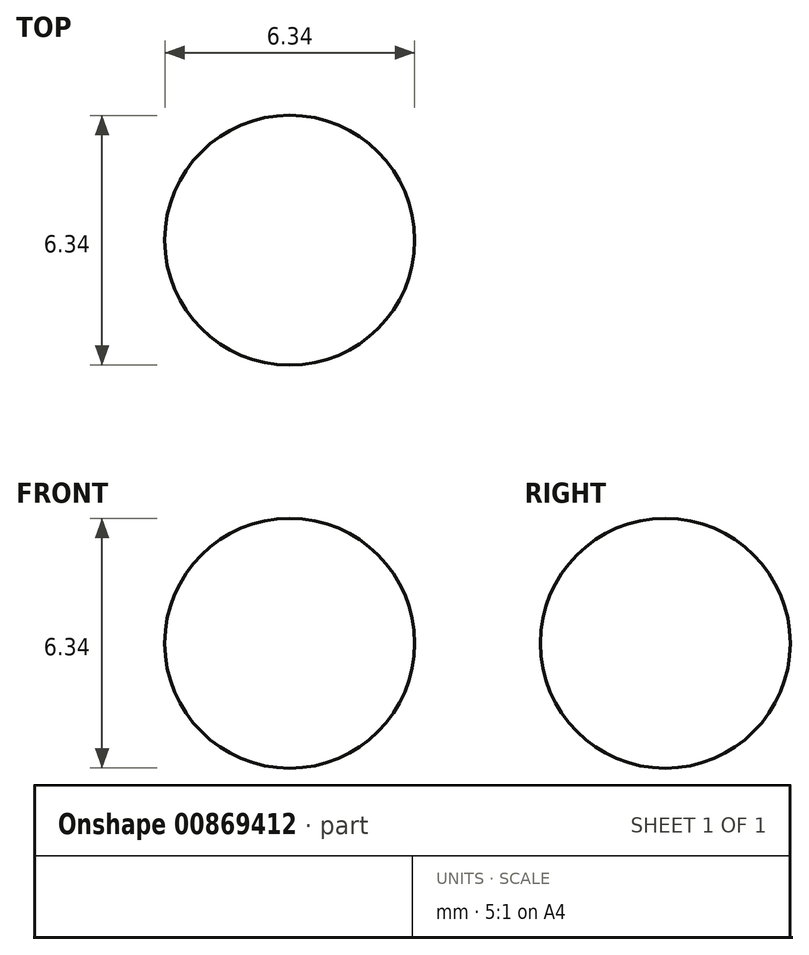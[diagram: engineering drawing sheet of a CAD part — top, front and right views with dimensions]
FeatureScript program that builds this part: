
annotation { "Feature Type Name" : "Feature", "Feature Type Description" : "" }
export const myFeature = defineFeature(function(context is Context, id is Id, definition is map)
    precondition{}
    {
        {
            var Q0;
            Q0=qCreatedBy(makeId("Front.planeOp"),FACE);
            var sketch = newSketch(context, id + "F0", { "sketchPlane" : qUnion([Q0])});
            skArc(sketch, "E0", {"start": v(0, -3.18) * mm, "mid": v(3.18, 0) * mm, "end": v(0, 3.18) * mm});
            skLineSegment(sketch, "E1", {"start": v(0, 3.18) * mm, "end": v(0, -3.18) * mm});
            skSolve(sketch);
        }
        {
            var Q0;
            Q0=makeQuery(id+"F0.imprint","IMPRINT",FACE,{"disambiguationData":[TD([[makeQuery(id+"F0.imprint","IMPRINT",EDGE,{"derivedFrom":sQuery(id+"F0.wireOp",EDGE,"E0")}),1.0]])]});
            var Q1;
            Q1=sQuery(id+"F0.wireOp",EDGE,"E1");
            revolve(context, id + "F1", {"surfaceOperationType" : NewSurfaceOperationType.NEW, "entities" : qUnion([Q0]), "axis" : qUnion([Q1]), "revolveType" : RevolveType.FULL});
        }
    });
